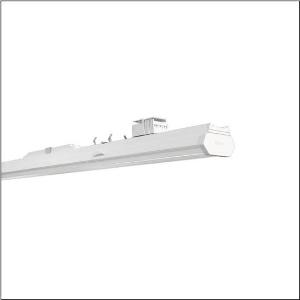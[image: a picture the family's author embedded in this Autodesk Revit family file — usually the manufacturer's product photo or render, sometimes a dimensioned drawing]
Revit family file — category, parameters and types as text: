
# Revit family: licross_r__21_protected_mo_52td11cn49xg_2815
name_source: partatom
category: Lighting Fixtures
units: mm (PartAtom-declared; Revit-internal decimal feet)

## family parameters
Cut with Voids When Loaded = No
Host = Face
Light Source = No
Part Type = Normal
Room Calculation Point = No
Round Connector Dimension = Use Diameter
Shared = No

## types (1)
- --- (1 x LED, 9070 lm, 50.4 W, 4000K)
    Apparent Load = 50 VA
    CIE Flux Codes = 83 94 98 100 100
    Color Rendering = 80
    Color Temperature = 4000K
    Default Elevation = 1800 mm
    Description = Licross® 21 Protected MO, luminaire insert, of sheet steel, galvanised, coil coated, white, length: 1.500mm, width: 90mm, height: 103mm, LED rated luminous flux: 9.080lm, light colour: 840, control gear: ON/OFF Multilumen, CLOi, control gear: ECG Multilumen, with plug, 3-pole, with phase selection, mains connection: 220..240V, AC, 50/60Hz, start of lifetime: 50W, end of service life: 61W, halogen-free wiring, primary light control with lens, of plastic, primary optical cover: cover, of PMMA, light emission: direct distribution, primary light characteristic: symmetric, protection rating (complete): IP54, insulation class (complete): insulation class I (protective earthing), certification: CE, ENEC, VDE, UKCA, protection symbol: D if used in an environment with non-conductive dust loads with corresponding accessories, impact resistance: IK06, permissible ambient temperature for indoor applications: -35..+45°C, corresponds to IFS (International Featured Standards) requirements for safety and quality in the food industry, reducing of maximum allowable ambient temperature of 5°C with ceiling mounting, LABS conformity tested according to VDMA 24364:2018-05, packaging unit: 1 piece
    Height = 92 mm
    Lamp = 1 x LED
    Lamp Light Flux = 9070 lm
    Lamp Power = 50.4 W
    Lamp count = 1
    Length = 1500 mm
    Luminous efficacy = 180 lm/W
    Manufacturer = Siteco
    ModVariant = No
    Model = 52TD11CN49XG
    Mounting Place = Ceiling
    Mounting Type = Pendant
    Number of Poles = 1
    OnlyDefault = Yes
    Power Factor = 1
    Product Name = Licross® 21 Protected MO
    Product group = luminaire insert
    ProductGroupID = 901
    Protection Class = Protection class I
    Protection Degree = IP 54
    RLX_Detail_Level = 1
    RLX_Emergency_Light_Flux = 0 lm
    RLX_Emergency_Type = 0
    RLX_Emergency_Type_DB = No
    RlxData = <blob elided: 21893 chars, md5=c57b5fc2>
    Socket = socket
    Standby Power = 0 W
    System Light Flux = 9070 lm
    System Power = 50 W
    Type Comments = factory setting: luminous flux: 100 % | (A | C | E) | 117 mA
    Type Image = l_1256148.jpg
    URL = http://relux.com
    VarID = @adj_040961
    Voltage = 0 V
    Weight = 0.00 kg
    Width = 88 mm

## geometry (parser evidence)
native form markers: Blend x4, Sweep x11
no freeform markers — native parametric forms only
